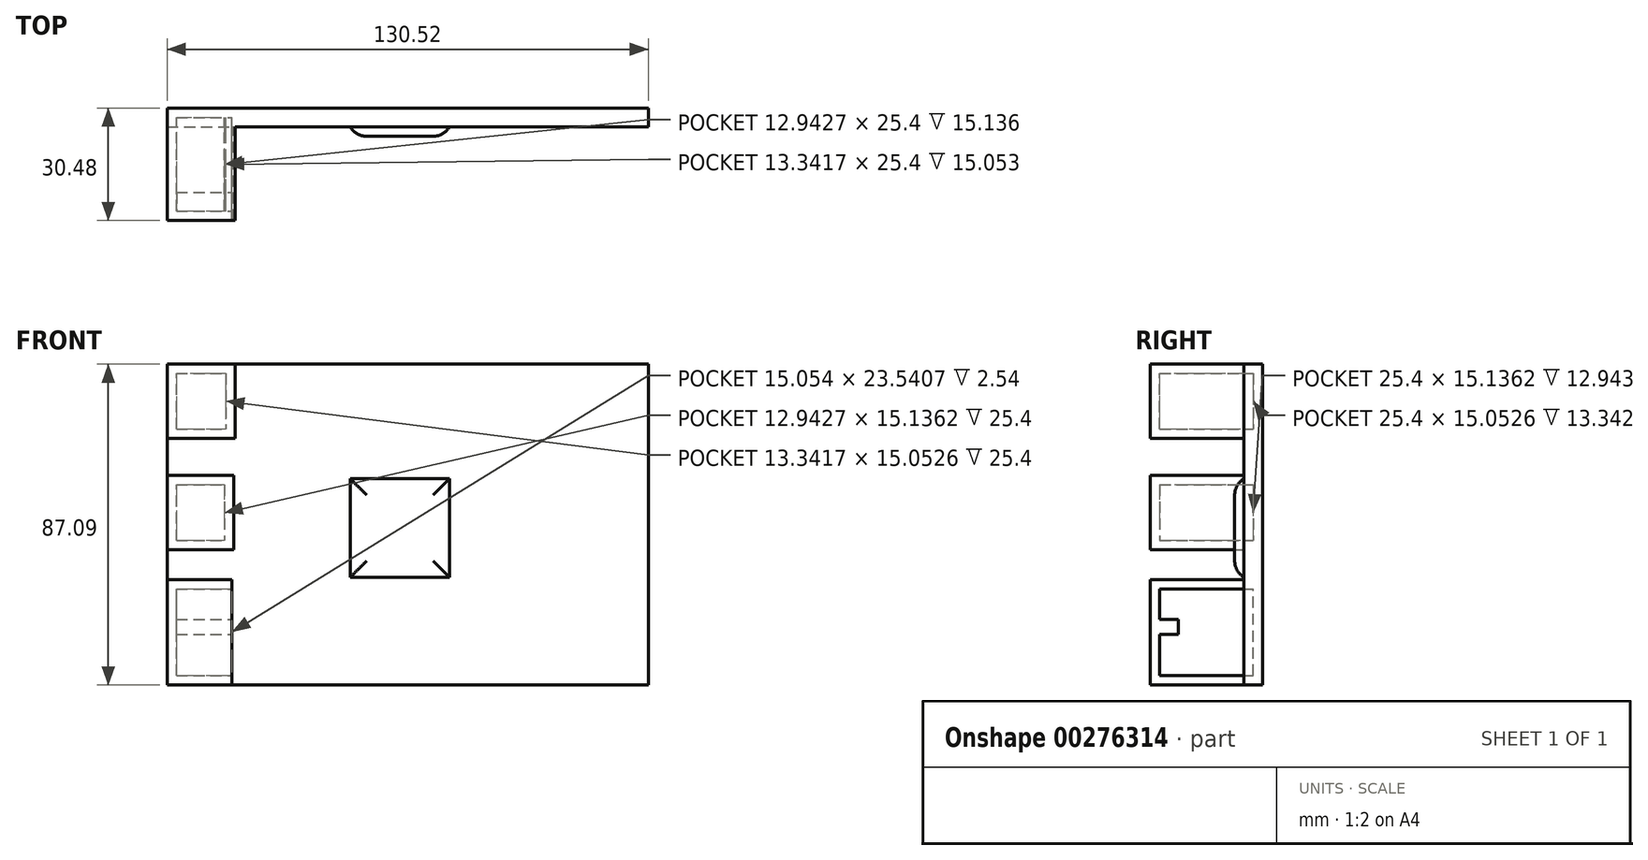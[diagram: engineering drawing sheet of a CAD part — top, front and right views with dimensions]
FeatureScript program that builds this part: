
annotation { "Feature Type Name" : "Feature", "Feature Type Description" : "" }
export const myFeature = defineFeature(function(context is Context, id is Id, definition is map)
    precondition{}
    {
        {
            var Q0;
            Q0=qCreatedBy(makeId("Front.planeOp"),FACE);
            var sketch = newSketch(context, id + "F0", { "sketchPlane" : qUnion([Q0])});
            skLineSegment(sketch, "E0.bottom", {"start": v(-63.12, -46.38) * mm, "end": v(67.4, -46.38) * mm});
            skLineSegment(sketch, "E0.top", {"start": v(-63.12, 40.71) * mm, "end": v(67.4, 40.71) * mm});
            skLineSegment(sketch, "E0.left", {"start": v(-63.12, -46.38) * mm, "end": v(-63.12, 40.71) * mm});
            skLineSegment(sketch, "E0.right", {"start": v(67.4, -46.38) * mm, "end": v(67.4, 40.71) * mm});
            skSolve(sketch);
        }
        {
            var Q0;
            Q0=makeQuery(id+"F0.imprint","IMPRINT",FACE,{"disambiguationData":[TD([[makeQuery(id+"F0.imprint","IMPRINT",EDGE,{"derivedFrom":sQuery(id+"F0.wireOp",EDGE,"E0.bottom")}),1.0]])]});
            extrude(context, id + "F1", {"entities" : qUnion([Q0]), "depth" : 5.08 * mm});
        }
        {
            var Q0;
            Q0=makeQuery(id+"F1.opExtrude","CAP_FACE",FACE,{"disambiguationData":[OSD([sQuery(id+"F0.wireOp",EDGE,"E0.bottom"),sQuery(id+"F0.wireOp",EDGE,"E0.top"),sQuery(id+"F0.wireOp",EDGE,"E0.left"),sQuery(id+"F0.wireOp",EDGE,"E0.right")])],"isStart":false});
            var sketch = newSketch(context, id + "F2", { "sketchPlane" : qUnion([Q0])});
            skLineSegment(sketch, "E1.bottom", {"start": v(-63.12, 40.71) * mm, "end": v(-44.7, 40.71) * mm});
            skLineSegment(sketch, "E1.top", {"start": v(-63.12, 20.58) * mm, "end": v(-44.7, 20.58) * mm});
            skLineSegment(sketch, "E1.left", {"start": v(-63.12, 40.71) * mm, "end": v(-63.12, 20.58) * mm});
            skLineSegment(sketch, "E1.right", {"start": v(-44.7, 40.71) * mm, "end": v(-44.7, 20.58) * mm});
            skSolve(sketch);
        }
        {
            var Q0;
            Q0=makeQuery(id+"F2.imprint","IMPRINT",FACE,{"disambiguationData":[TD([[makeQuery(id+"F2.imprint","IMPRINT",EDGE,{"derivedFrom":sQuery(id+"F2.wireOp",EDGE,"E1.bottom")}),-1.0]])]});
            extrude(context, id + "F3", {"entities" : qUnion([Q0]), "operationType" : NewBodyOperationType.ADD, "depth" : 25.4 * mm});
        }
        {
            var Q0;
            Q0=makeQuery(id+"F1.opExtrude","CAP_FACE",FACE,{"disambiguationData":[OSD([sQuery(id+"F0.wireOp",EDGE,"E0.bottom"),sQuery(id+"F0.wireOp",EDGE,"E0.top"),sQuery(id+"F0.wireOp",EDGE,"E0.left"),sQuery(id+"F0.wireOp",EDGE,"E0.right")])],"isStart":false});
            var sketch = newSketch(context, id + "F4", { "sketchPlane" : qUnion([Q0])});
            skLineSegment(sketch, "E2.bottom", {"start": v(-63.12, 10.52) * mm, "end": v(-45.1, 10.52) * mm});
            skLineSegment(sketch, "E2.top", {"start": v(-63.12, -9.7) * mm, "end": v(-45.1, -9.7) * mm});
            skLineSegment(sketch, "E2.left", {"start": v(-63.12, 10.52) * mm, "end": v(-63.12, -9.7) * mm});
            skLineSegment(sketch, "E2.right", {"start": v(-45.1, 10.52) * mm, "end": v(-45.1, -9.7) * mm});
            skSolve(sketch);
        }
        {
            var Q0;
            Q0=makeQuery(id+"F4.imprint","IMPRINT",FACE,{"disambiguationData":[TD([[makeQuery(id+"F4.imprint","IMPRINT",EDGE,{"derivedFrom":sQuery(id+"F4.wireOp",EDGE,"E2.bottom")}),-1.0]])]});
            extrude(context, id + "F5", {"entities" : qUnion([Q0]), "operationType" : NewBodyOperationType.ADD, "depth" : 25.4 * mm});
        }
        {
            var Q0;
            Q0=makeQuery(id+"F1.opExtrude","CAP_FACE",FACE,{"disambiguationData":[OSD([sQuery(id+"F0.wireOp",EDGE,"E0.bottom"),sQuery(id+"F0.wireOp",EDGE,"E0.top"),sQuery(id+"F0.wireOp",EDGE,"E0.left"),sQuery(id+"F0.wireOp",EDGE,"E0.right")])],"isStart":false});
            var sketch = newSketch(context, id + "F6", { "sketchPlane" : qUnion([Q0])});
            skLineSegment(sketch, "E3.bottom", {"start": v(-63.12, -17.76) * mm, "end": v(-45.52, -17.76) * mm});
            skLineSegment(sketch, "E3.top", {"start": v(-63.12, -46.38) * mm, "end": v(-45.52, -46.38) * mm});
            skLineSegment(sketch, "E3.left", {"start": v(-63.12, -17.76) * mm, "end": v(-63.12, -46.38) * mm});
            skLineSegment(sketch, "E3.right", {"start": v(-45.52, -17.76) * mm, "end": v(-45.52, -46.38) * mm});
            skSolve(sketch);
        }
        {
            var Q0;
            Q0=makeQuery(id+"F6.imprint","IMPRINT",FACE,{"disambiguationData":[TD([[makeQuery(id+"F6.imprint","IMPRINT",EDGE,{"derivedFrom":sQuery(id+"F6.wireOp",EDGE,"E3.bottom")}),-1.0]])]});
            extrude(context, id + "F7", {"entities" : qUnion([Q0]), "operationType" : NewBodyOperationType.ADD, "depth" : 25.4 * mm});
        }
        {
            var Q0;
            Q0=makeQuery(id+"F7.opExtrude","SWEPT_FACE",FACE,{"disambiguationData":[OSD([sQuery(id+"F6.wireOp",EDGE,"E3.right")])]});
            shell(context, id + "F8", {"entities" : qUnion([Q0]), "thickness" : 2.54 * mm});
        }
        {
            var Q0;
            Q0=makeQuery(id+"F8.opShell","OFFSET_FACE",FACE,{"disambiguationData":[OSD([sQuery(id+"F6.wireOp",EDGE,"E3.bottom"),sQuery(id+"F6.wireOp",EDGE,"E3.top"),sQuery(id+"F6.wireOp",EDGE,"E3.left"),sQuery(id+"F6.wireOp",EDGE,"E3.right")])]});
            var sketch = newSketch(context, id + "F9", { "sketchPlane" : qUnion([Q0])});
            skLineSegment(sketch, "E4.bottom", {"start": v(60.58, -32.68) * mm, "end": v(45.52, -32.68) * mm});
            skLineSegment(sketch, "E4.top", {"start": v(60.58, -28.6) * mm, "end": v(45.52, -28.6) * mm});
            skLineSegment(sketch, "E4.left", {"start": v(60.58, -32.68) * mm, "end": v(60.58, -28.6) * mm});
            skLineSegment(sketch, "E4.right", {"start": v(45.52, -32.68) * mm, "end": v(45.52, -28.6) * mm});
            skSolve(sketch);
        }
        {
            var Q0;
            Q0=makeQuery(id+"F9.imprint","IMPRINT",FACE,{"disambiguationData":[TD([[makeQuery(id+"F9.imprint","IMPRINT",EDGE,{"derivedFrom":sQuery(id+"F9.wireOp",EDGE,"E4.bottom")}),-1.0]])]});
            extrude(context, id + "F10", {"entities" : qUnion([Q0]), "operationType" : NewBodyOperationType.ADD, "depth" : 5.08 * mm});
        }
        {
            var Q0;
            Q0=makeQuery(id+"F1.opExtrude","CAP_FACE",FACE,{"disambiguationData":[OSD([sQuery(id+"F0.wireOp",EDGE,"E0.bottom"),sQuery(id+"F0.wireOp",EDGE,"E0.top"),sQuery(id+"F0.wireOp",EDGE,"E0.left"),sQuery(id+"F0.wireOp",EDGE,"E0.right")])],"isStart":false});
            var sketch = newSketch(context, id + "F11", { "sketchPlane" : qUnion([Q0])});
            skLineSegment(sketch, "E5.bottom", {"start": v(13.44, 9.6) * mm, "end": v(-13.44, 9.6) * mm});
            skLineSegment(sketch, "E5.top", {"start": v(13.44, -17.14) * mm, "end": v(-13.44, -17.14) * mm});
            skLineSegment(sketch, "E5.left", {"start": v(13.44, 9.6) * mm, "end": v(13.44, -17.14) * mm});
            skLineSegment(sketch, "E5.right", {"start": v(-13.44, 9.6) * mm, "end": v(-13.44, -17.14) * mm});
            skPoint(sketch, "E5.middle", {"position": v(0, -3.77) * mm});
            skSolve(sketch);
        }
        {
            var Q0;
            Q0=makeQuery(id+"F11.imprint","IMPRINT",FACE,{"disambiguationData":[TD([[makeQuery(id+"F11.imprint","IMPRINT",EDGE,{"derivedFrom":sQuery(id+"F11.wireOp",EDGE,"E5.bottom")}),1.0]])]});
            extrude(context, id + "F12", {"entities" : qUnion([Q0]), "operationType" : NewBodyOperationType.ADD, "depth" : 2.54 * mm});
        }
        {
            var Q0;
            Q0=makeQuery(id+"F12.opExtrude","CAP_EDGE",EDGE,{"disambiguationData":[OSD([sQuery(id+"F11.wireOp",EDGE,"E5.top")])],"isStart":false});
            var Q1;
            Q1=makeQuery(id+"F12.opExtrude","CAP_EDGE",EDGE,{"disambiguationData":[OSD([sQuery(id+"F11.wireOp",EDGE,"E5.right")])],"isStart":false});
            var Q2;
            Q2=makeQuery(id+"F12.opExtrude","CAP_EDGE",EDGE,{"disambiguationData":[OSD([sQuery(id+"F11.wireOp",EDGE,"E5.bottom")])],"isStart":false});
            var Q3;
            Q3=makeQuery(id+"F12.opExtrude","CAP_EDGE",EDGE,{"disambiguationData":[OSD([sQuery(id+"F11.wireOp",EDGE,"E5.left")])],"isStart":false});
            fillet(context, id + "F13", {"entities" : qUnion([Q0, Q1, Q2, Q3]), "radius" : 5.08 * mm, "tangentPropagation" : true, "allowEdgeOverflow" : false});
        }
    });
